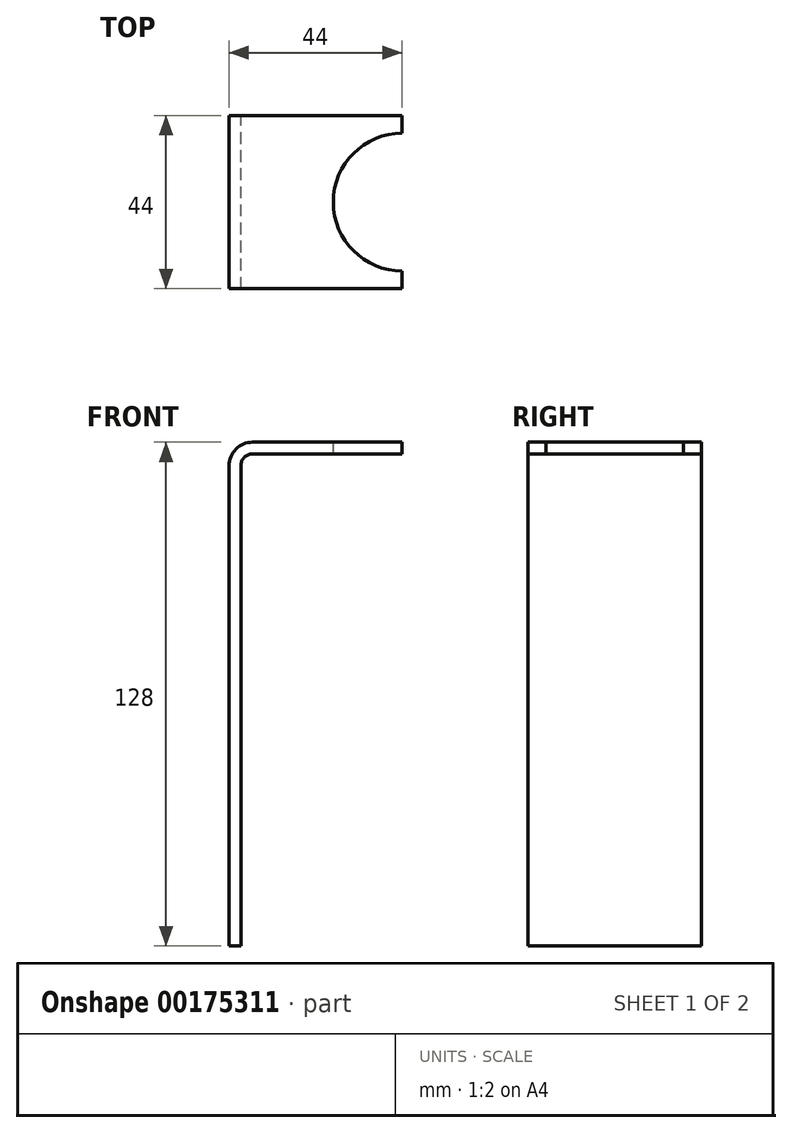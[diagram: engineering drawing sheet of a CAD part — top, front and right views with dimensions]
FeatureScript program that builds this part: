
annotation { "Feature Type Name" : "Feature", "Feature Type Description" : "" }
export const myFeature = defineFeature(function(context is Context, id is Id, definition is map)
    precondition{}
    {
        {
            var Q0;
            Q0=qCreatedBy(makeId("Front.planeOp"),FACE);
            var sketch = newSketch(context, id + "F0", { "sketchPlane" : qUnion([Q0])});
            skLineSegment(sketch, "E0", {"start": v(0, 0) * mm, "end": v(0, 122) * mm});
            skLineSegment(sketch, "E1", {"start": v(3, 125) * mm, "end": v(41, 125) * mm});
            skLineSegment(sketch, "E2.0", {"start": v(3, 128) * mm, "end": v(41, 128) * mm});
            skLineSegment(sketch, "E2.1", {"start": v(-3, 0) * mm, "end": v(-3, 122) * mm});
            skLineSegment(sketch, "E3", {"start": v(41, 128) * mm, "end": v(41, 125) * mm});
            skLineSegment(sketch, "E4", {"start": v(-3, 0) * mm, "end": v(0, 0) * mm});
            skPoint(sketch, "E5.visualSharp", {"position": v(-3, 128) * mm});
            skArc(sketch, "E5.filletArc", {"start": v(3, 128) * mm, "mid": v(-1.24, 126.24) * mm, "end": v(-3, 122) * mm});
            skPoint(sketch, "E6.visualSharp", {"position": v(0, 125) * mm});
            skArc(sketch, "E6.filletArc", {"start": v(3, 125) * mm, "mid": v(0.88, 124.12) * mm, "end": v(0, 122) * mm});
            skSolve(sketch);
        }
        {
            var Q0;
            Q0=makeQuery(id+"F0.imprint","IMPRINT",FACE,{"disambiguationData":[TD([[makeQuery(id+"F0.imprint","IMPRINT",EDGE,{"derivedFrom":sQuery(id+"F0.wireOp",EDGE,"E0")}),1.0]])]});
            extrude(context, id + "F1", {"entities" : qUnion([Q0]), "depth" : 44 * mm});
        }
        {
            var Q0;
            Q0=makeQuery(id+"F1.opExtrude","SWEPT_FACE",FACE,{"disambiguationData":[OSD([sQuery(id+"F0.wireOp",EDGE,"E2.0")])]});
            var sketch = newSketch(context, id + "F2", { "sketchPlane" : qUnion([Q0])});
            skLineSegment(sketch, "E7", {"start": v(41, -22) * mm, "end": v(3, -22) * mm, "construction": true});
            skSolve(sketch);
        }
        {
            var Q0;
            Q0=sQuery(id+"F2.wireOp",VERTEX,"E7.start");
            var Q1;
            Q1=makeQuery(id+"F1.opExtrude","SWEPT_BODY",BODY,{"disambiguationData":[OSD([sQuery(id+"F0.wireOp",EDGE,"E0"),sQuery(id+"F0.wireOp",EDGE,"E1"),sQuery(id+"F0.wireOp",EDGE,"E2.0"),sQuery(id+"F0.wireOp",EDGE,"E2.1"),sQuery(id+"F0.wireOp",EDGE,"E3"),sQuery(id+"F0.wireOp",EDGE,"E4"),sQuery(id+"F0.wireOp",EDGE,"E5.filletArc"),sQuery(id+"F0.wireOp",EDGE,"E6.filletArc")])]});
            hole(context, id + "F3", {"style" : HoleStyle.SIMPLE, "endStyle" : HoleEndStyle.THROUGH, "holeDiameter" : 35 * mm, "locations" : qUnion([Q0]), "scope" : qUnion([Q1]), "isTappedThrough" : true});
        }
    });
